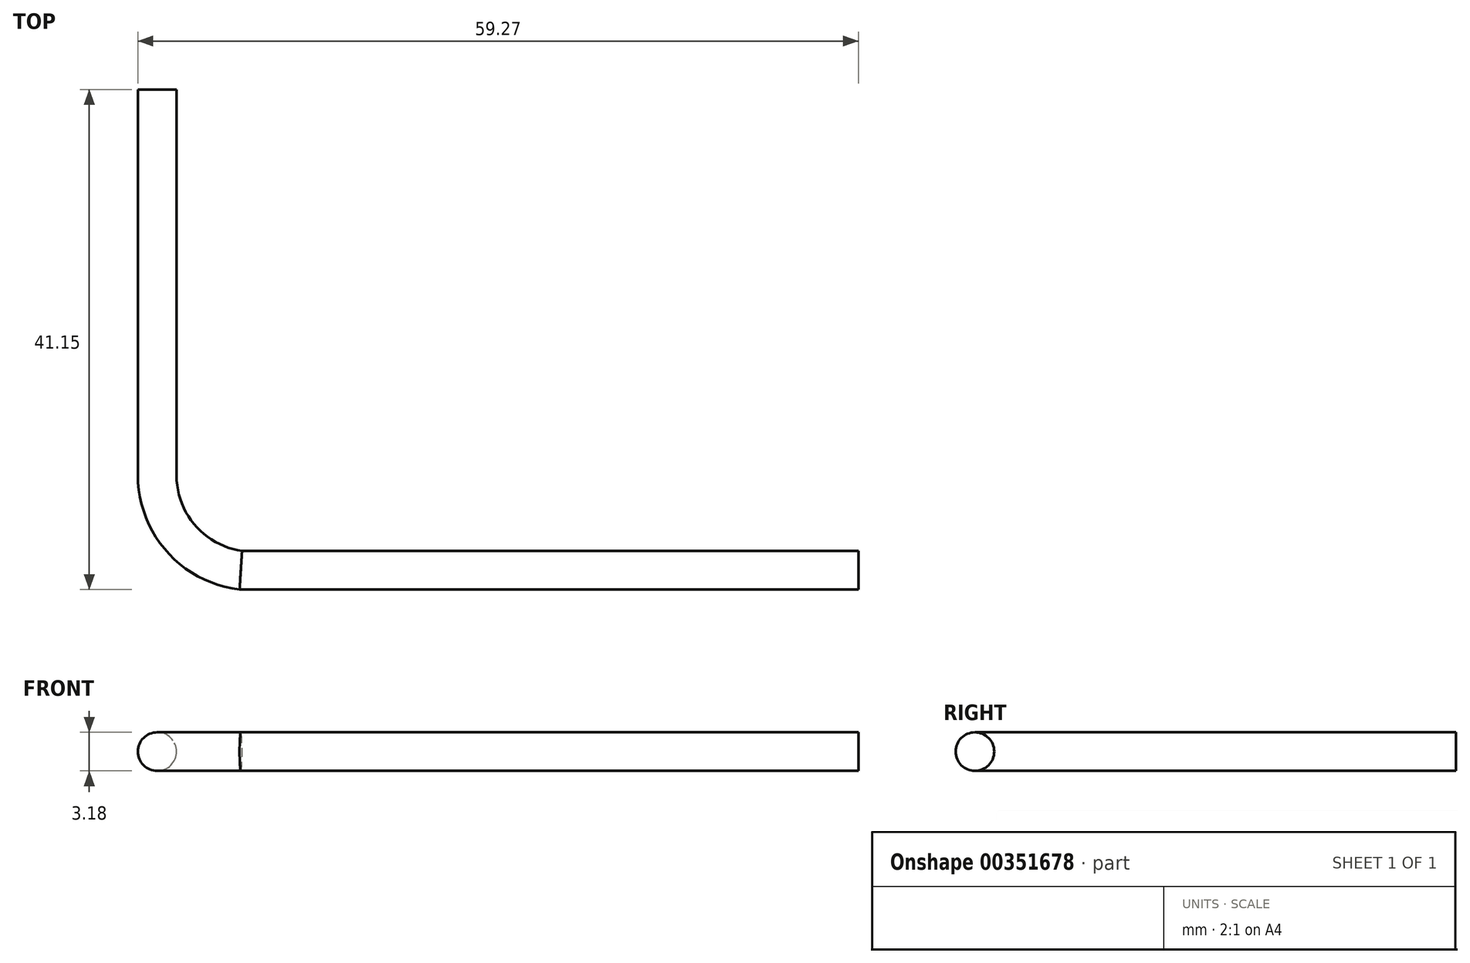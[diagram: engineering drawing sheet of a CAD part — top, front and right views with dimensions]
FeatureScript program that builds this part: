
annotation { "Feature Type Name" : "Feature", "Feature Type Description" : "" }
export const myFeature = defineFeature(function(context is Context, id is Id, definition is map)
    precondition{}
    {
        {
            var Q0;
            Q0=qCreatedBy(makeId("Front.planeOp"),FACE);
            var sketch = newSketch(context, id + "F0", { "sketchPlane" : qUnion([Q0])});
            skCircle(sketch, "E0", {"center": v(0, 0) * mm, "radius": 1.59 * mm});
            skSolve(sketch);
        }
        {
            var Q0;
            Q0=qCreatedBy(makeId("Top.planeOp"),FACE);
            var sketch = newSketch(context, id + "F1", { "sketchPlane" : qUnion([Q0])});
            skLineSegment(sketch, "E1", {"start": v(0, 0) * mm, "end": v(0, -31.75) * mm});
            skArc(sketch, "E2", {"start": v(0, -31.75) * mm, "mid": v(1.96, -36.95) * mm, "end": v(6.88, -39.56) * mm});
            skLineSegment(sketch, "E3", {"start": v(6.88, -39.56) * mm, "end": v(57.68, -39.56) * mm});
            skSolve(sketch);
        }
        {
            var Q0;
            Q0=makeQuery(id+"F0.imprint","IMPRINT",FACE,{"disambiguationData":[TD([[makeQuery(id+"F0.imprint","IMPRINT",EDGE,{"derivedFrom":sQuery(id+"F0.wireOp",EDGE,"E0")}),1.0]])]});
            var Q1;
            Q1=sQuery(id+"F1.wireOp",EDGE,"E1");
            var Q2;
            Q2=sQuery(id+"F1.wireOp",EDGE,"E2");
            var Q3;
            Q3=sQuery(id+"F1.wireOp",EDGE,"E3");
            sweep(context, id + "F2", {"profiles" : qUnion([Q0]), "path" : qUnion([Q1, Q2, Q3])});
        }
    });
